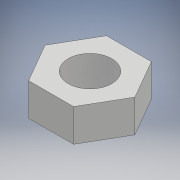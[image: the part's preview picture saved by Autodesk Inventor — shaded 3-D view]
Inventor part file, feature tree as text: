
AUTODESK INVENTOR PART (.ipt)
format: ipt  version: 2018.3 (Build 223284000, 284)  size: 97,280 bytes
history: native  units: mm
features: extrude x1, sketch x1
ambient origin geometry x8: Origin, YZ Plane, XZ Plane, XY Plane, X Axis, Y Axis, Z Axis, Center Point
bodies: Solid1 (feature_tree)
feature tree (2):
  extrude  "Extrusion1"  Depth=3.0mm
  sketch  "Sketch1"  dims[d0=7.15mm d1=4.0mm d2=3.0mm d3=0.0mm]
